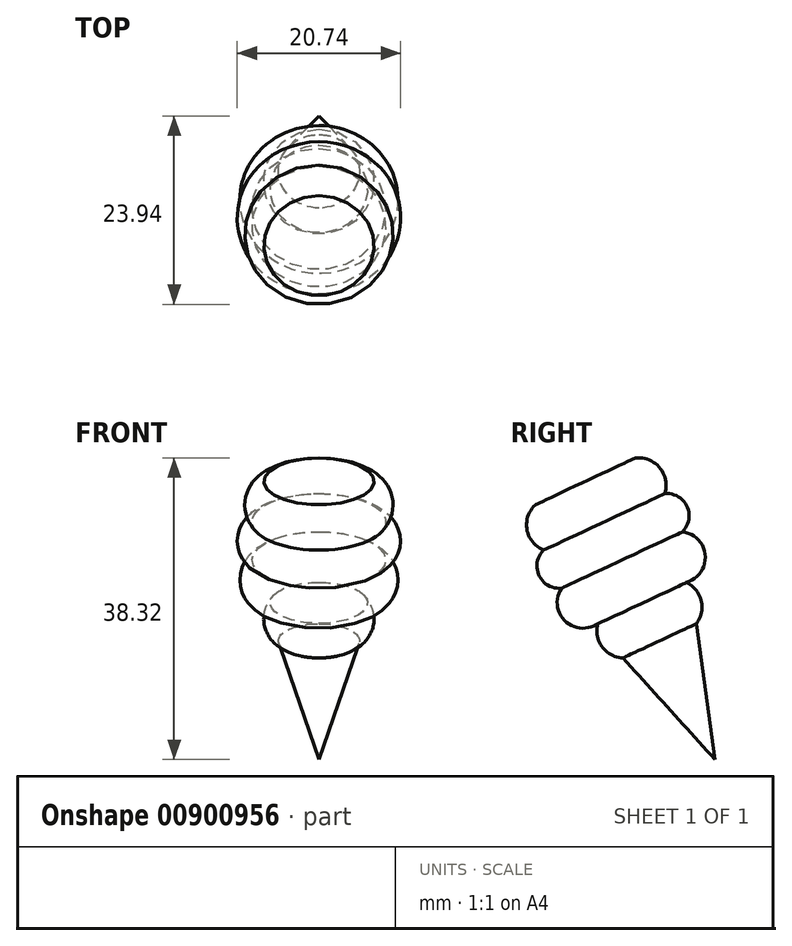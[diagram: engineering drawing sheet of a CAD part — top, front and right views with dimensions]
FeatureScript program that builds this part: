
annotation { "Feature Type Name" : "Feature", "Feature Type Description" : "" }
export const myFeature = defineFeature(function(context is Context, id is Id, definition is map)
    precondition{}
    {
        {
            var Q0;
            Q0=qCreatedBy(makeId("Right.planeOp"),FACE);
            var sketch = newSketch(context, id + "F0", { "sketchPlane" : qUnion([Q0])});
            skLineSegment(sketch, "E0", {"start": v(0, -38.98) * mm, "end": v(-11.7, -26.07) * mm});
            skLineSegment(sketch, "E1", {"start": v(-11.7, -26.07) * mm, "end": v(-7.03, -23.9) * mm});
            skLineSegment(sketch, "E2", {"start": v(-7.03, -23.9) * mm, "end": v(0, -38.98) * mm});
            skArc(sketch, "E3", {"start": v(-14.88, -21.68) * mm, "mid": v(-14.34, -24.64) * mm, "end": v(-11.7, -26.07) * mm});
            skArc(sketch, "E4", {"start": v(-19.5, -17.22) * mm, "mid": v(-19.05, -21.37) * mm, "end": v(-14.88, -21.68) * mm});
            skArc(sketch, "E5", {"start": v(-21.76, -12.37) * mm, "mid": v(-22.35, -15.6) * mm, "end": v(-19.5, -17.22) * mm});
            skArc(sketch, "E6", {"start": v(-22.82, -6.61) * mm, "mid": v(-23.88, -9.78) * mm, "end": v(-21.76, -12.37) * mm});
            skLineSegment(sketch, "E7", {"start": v(-7.03, -23.9) * mm, "end": v(-16.47, -3.65) * mm});
            skLineSegment(sketch, "E8", {"start": v(-16.47, -3.65) * mm, "end": v(-22.82, -6.61) * mm});
            skLineSegment(sketch, "E9", {"start": v(-21.76, -12.37) * mm, "end": v(-14.08, -8.79) * mm});
            skLineSegment(sketch, "E10", {"start": v(-19.5, -17.22) * mm, "end": v(-11.82, -13.63) * mm});
            skLineSegment(sketch, "E11", {"start": v(-14.88, -21.68) * mm, "end": v(-9.28, -19.07) * mm});
            skLineSegment(sketch, "E12.0", {"start": v(-7.03, -23.9) * mm, "end": v(-14.08, -8.79) * mm, "construction": true});
            skLineSegment(sketch, "E13.0", {"start": v(-19.5, -17.22) * mm, "end": v(-21.76, -12.37) * mm, "construction": true});
            skSolve(sketch);
        }
        {
            var Q0;
            Q0=makeQuery(id+"F0.imprint","IMPRINT",FACE,{"disambiguationData":[TD([[makeQuery(id+"F0.imprint","IMPRINT",EDGE,{"derivedFrom":sQuery(id+"F0.wireOp",EDGE,"E6")}),1.0]])]});
            var Q1;
            Q1=makeQuery(id+"F0.imprint","IMPRINT",FACE,{"disambiguationData":[TD([[makeQuery(id+"F0.imprint","IMPRINT",EDGE,{"derivedFrom":sQuery(id+"F0.wireOp",EDGE,"E5")}),1.0]])]});
            var Q2;
            Q2=makeQuery(id+"F0.imprint","IMPRINT",FACE,{"disambiguationData":[TD([[makeQuery(id+"F0.imprint","IMPRINT",EDGE,{"derivedFrom":sQuery(id+"F0.wireOp",EDGE,"E4")}),1.0]])]});
            var Q3;
            {var subQ0=sQuery(id+"F0.wireOp",EDGE,"E1");Q3=makeQuery(id+"F0.imprint","IMPRINT",FACE,{"disambiguationData":[TD([[makeQuery(id+"F0.imprint","IMPRINT",EDGE,{"derivedFrom":subQ0}),1.0]])]});}
            var Q4;
            Q4=makeQuery(id+"F0.imprint","IMPRINT",FACE,{"disambiguationData":[TD([[makeQuery(id+"F0.imprint","IMPRINT",EDGE,{"derivedFrom":sQuery(id+"F0.wireOp",EDGE,"E0")}),-1.0]])]});
            var Q5;
            Q5=sQuery(id+"F0.wireOp",EDGE,"E7");
            revolve(context, id + "F1", {"surfaceOperationType" : NewSurfaceOperationType.NEW, "entities" : qUnion([Q0, Q1, Q2, Q3, Q4]), "axis" : qUnion([Q5]), "revolveType" : RevolveType.FULL});
        }
    });
